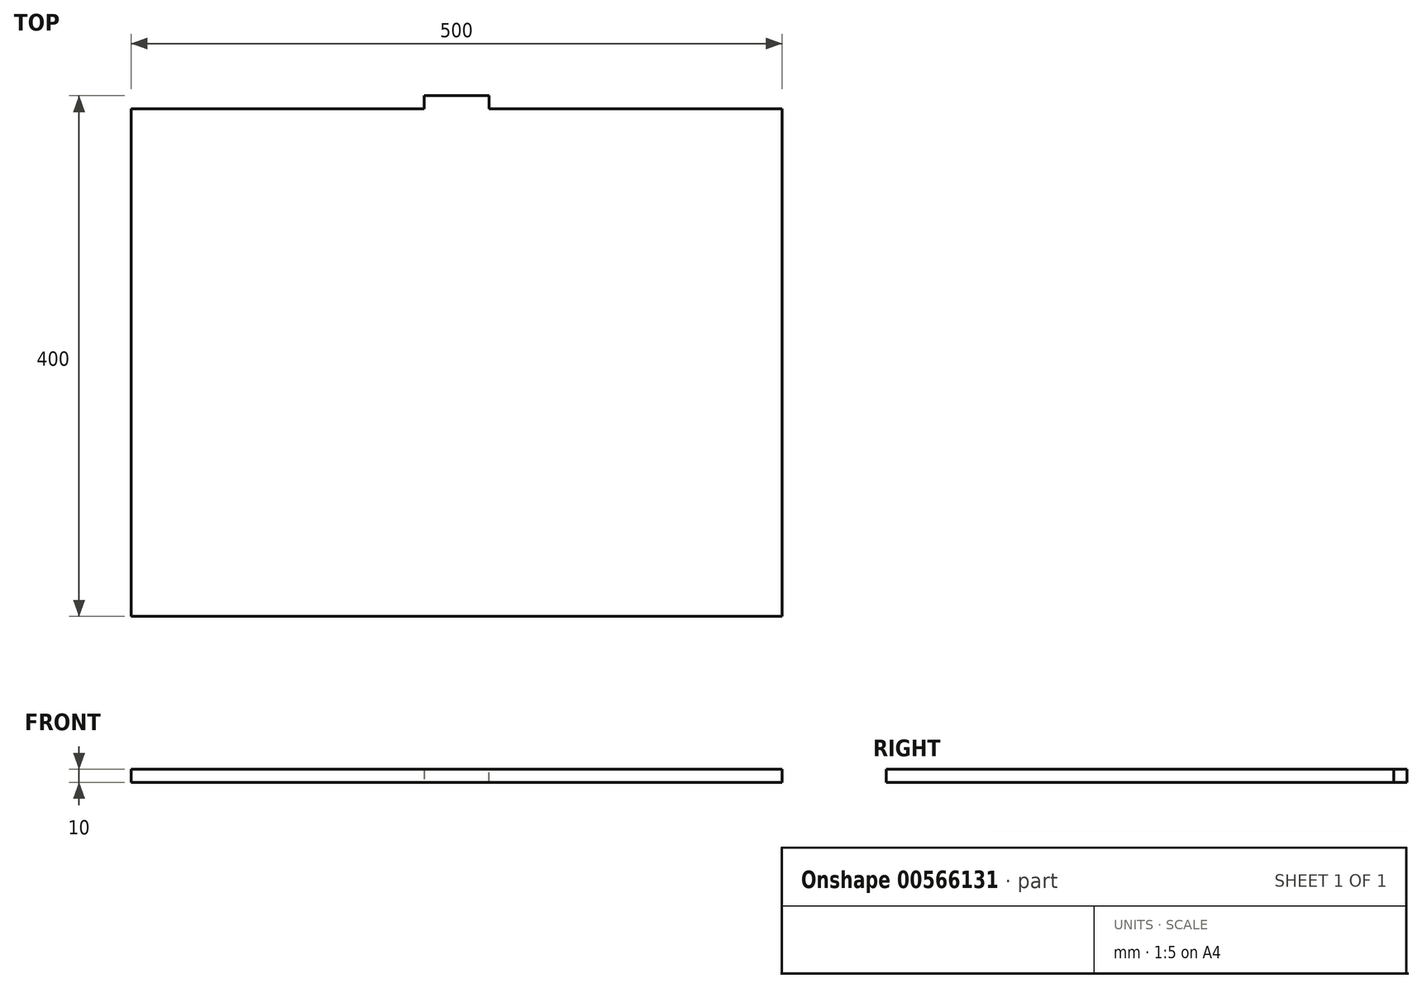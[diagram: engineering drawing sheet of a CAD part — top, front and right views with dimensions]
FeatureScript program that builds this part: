
annotation { "Feature Type Name" : "Feature", "Feature Type Description" : "" }
export const myFeature = defineFeature(function(context is Context, id is Id, definition is map)
    precondition{}
    {
        {
            var Q0;
            Q0=qCreatedBy(makeId("Front.planeOp"),FACE);
            var sketch = newSketch(context, id + "F0", { "sketchPlane" : qUnion([Q0])});
            skLineSegment(sketch, "E0.left", {"start": v(-250, 60) * mm, "end": v(-250, 50) * mm});
            skLineSegment(sketch, "E0.right", {"start": v(250, 60) * mm, "end": v(250, 50) * mm});
            skLineSegment(sketch, "E1", {"start": v(-250, 60) * mm, "end": v(250, 60) * mm});
            skLineSegment(sketch, "E2", {"start": v(250, 50) * mm, "end": v(-250, 50) * mm});
            skLineSegment(sketch, "E3", {"start": v(-250, 50) * mm, "end": v(-250, 60) * mm});
            skSolve(sketch);
        }
        {
            var Q0;
            Q0=makeQuery(id+"F0.imprint","IMPRINT",FACE,{"disambiguationData":[TD([[makeQuery(id+"F0.imprint","IMPRINT",EDGE,{"derivedFrom":sQuery(id+"F0.wireOp",EDGE,"E1")}),-1.0]])]});
            extrude(context, id + "F1", {"entities" : qUnion([Q0]), "depth" : 390 * mm, "offsetDistance" : 25 * mm});
        }
        {
            var Q0;
            Q0=makeQuery(id+"F1.opExtrude","CAP_FACE",FACE,{"disambiguationData":[OSD([sQuery(id+"F0.wireOp",EDGE,"E1"),sQuery(id+"F0.wireOp",EDGE,"E0.right"),sQuery(id+"F0.wireOp",EDGE,"E2"),sQuery(id+"F0.wireOp",EDGE,"E3")])],"isStart":true});
            var sketch = newSketch(context, id + "F2", { "sketchPlane" : qUnion([Q0])});
            skLineSegment(sketch, "E4", {"start": v(25, 60) * mm, "end": v(25, 50) * mm});
            skLineSegment(sketch, "E5", {"start": v(-25, 50) * mm, "end": v(-25, 60) * mm});
            skLineSegment(sketch, "E6", {"start": v(-25, 60) * mm, "end": v(25, 60) * mm});
            skLineSegment(sketch, "E7", {"start": v(25, 50) * mm, "end": v(-25, 50) * mm});
            skSolve(sketch);
        }
        {
            var Q0;
            Q0 = qSketchRegion(id + "F2", true);
            extrude(context, id + "F3", {"entities" : qUnion([Q0]), "operationType" : NewBodyOperationType.ADD, "depth" : 10 * mm, "offsetDistance" : 25 * mm});
        }
    });
